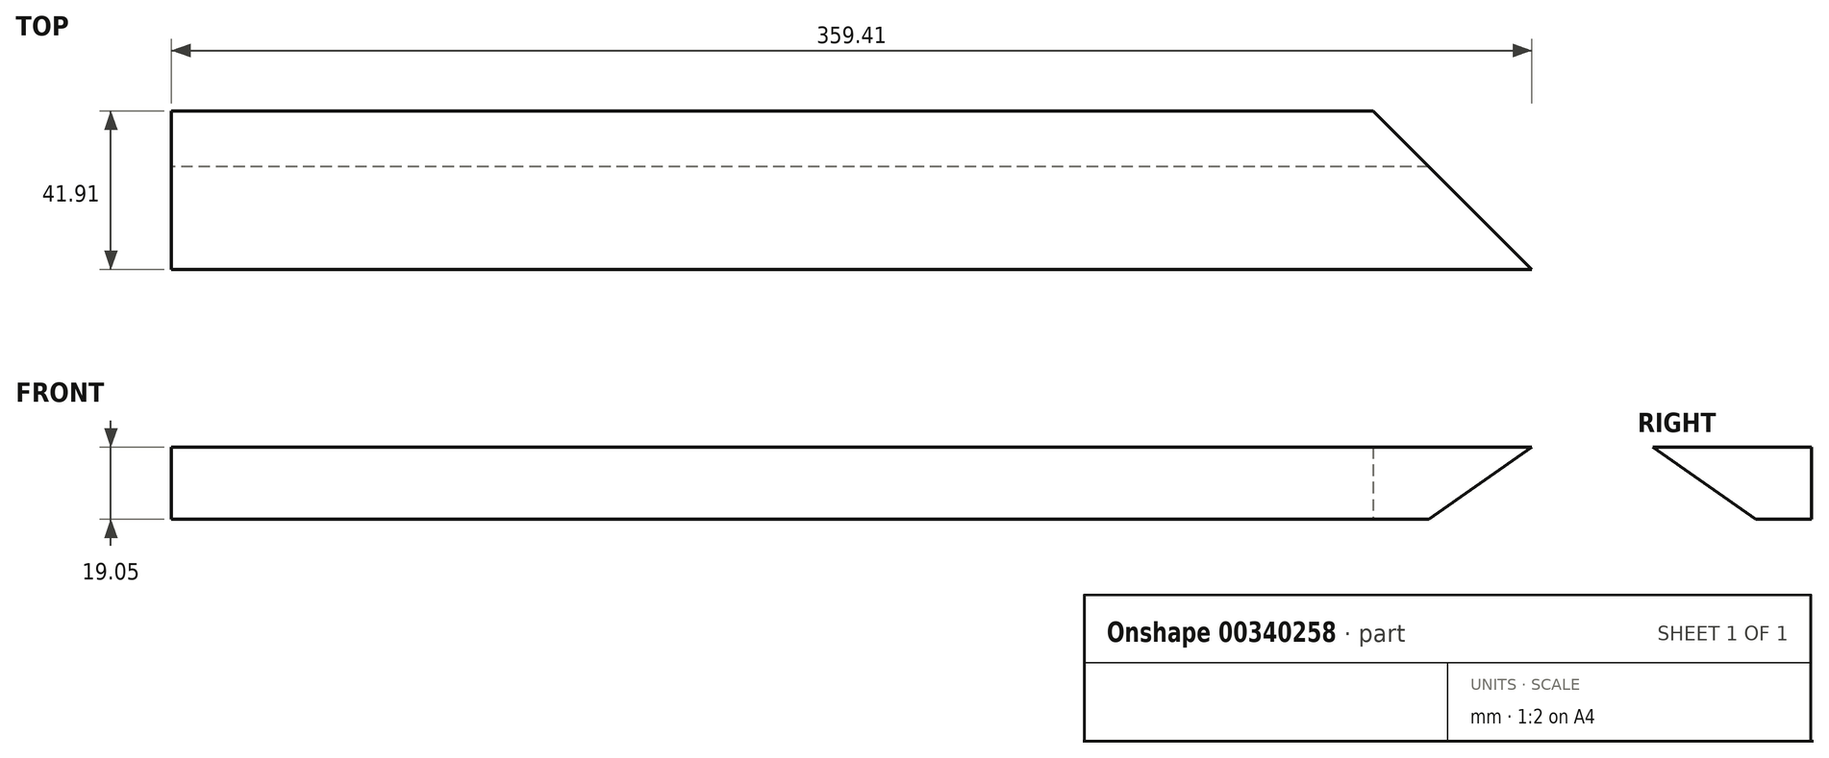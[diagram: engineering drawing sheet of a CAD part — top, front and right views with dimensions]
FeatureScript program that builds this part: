
annotation { "Feature Type Name" : "Feature", "Feature Type Description" : "" }
export const myFeature = defineFeature(function(context is Context, id is Id, definition is map)
    precondition{}
    {
        {
            var Q0;
            Q0=qCreatedBy(makeId("Right.planeOp"),FACE);
            var sketch = newSketch(context, id + "F0", { "sketchPlane" : qUnion([Q0])});
            skLineSegment(sketch, "E0.bottom", {"start": v(0, 19.05) * mm, "end": v(-41.91, 19.05) * mm});
            skLineSegment(sketch, "E0.top", {"start": v(0, 0) * mm, "end": v(-14.7, 0) * mm});
            skLineSegment(sketch, "E0.left", {"start": v(0, 19.05) * mm, "end": v(0, 0) * mm});
            skPoint(sketch, "E0.middle", {"position": v(0, 0) * mm});
            skLineSegment(sketch, "E1", {"start": v(-41.91, 19.05) * mm, "end": v(-14.7, 0) * mm});
            skSolve(sketch);
        }
        {
            var Q0;
            Q0=qSketchRegion(id+"F0",true);
            extrude(context, id + "F1", {"entities" : qUnion([Q0]), "depth" : 228.6 * mm, "hasSecondDirection" : true, "secondDirectionOppositeDirection" : true, "secondDirectionDepth" : 228.6 * mm});
        }
        {
            var Q0;
            Q0=qCreatedBy(makeId("Top.planeOp"),FACE);
            var sketch = newSketch(context, id + "F2", { "sketchPlane" : qUnion([Q0])});
            skLineSegment(sketch, "E2", {"start": v(-88.9, 0) * mm, "end": v(88.9, 0) * mm, "construction": true});
            skLineSegment(sketch, "E3", {"start": v(0, 0) * mm, "end": v(0, -29.83) * mm, "construction": true});
            skLineSegment(sketch, "E4", {"start": v(88.9, 0) * mm, "end": v(238.76, 0) * mm});
            skLineSegment(sketch, "E5", {"start": v(238.76, 0) * mm, "end": v(238.76, -149.86) * mm});
            skLineSegment(sketch, "E6", {"start": v(238.76, -149.86) * mm, "end": v(88.9, 0) * mm});
            skSolve(sketch);
        }
        {
            var Q0;
            Q0=qSketchRegion(id+"F2",true);
            extrude(context, id + "F3", {"entities" : qUnion([Q0]), "operationType" : NewBodyOperationType.REMOVE, "endBound" : BoundingType.THROUGH_ALL, "depth" : 25.4 * mm});
        }
    });
